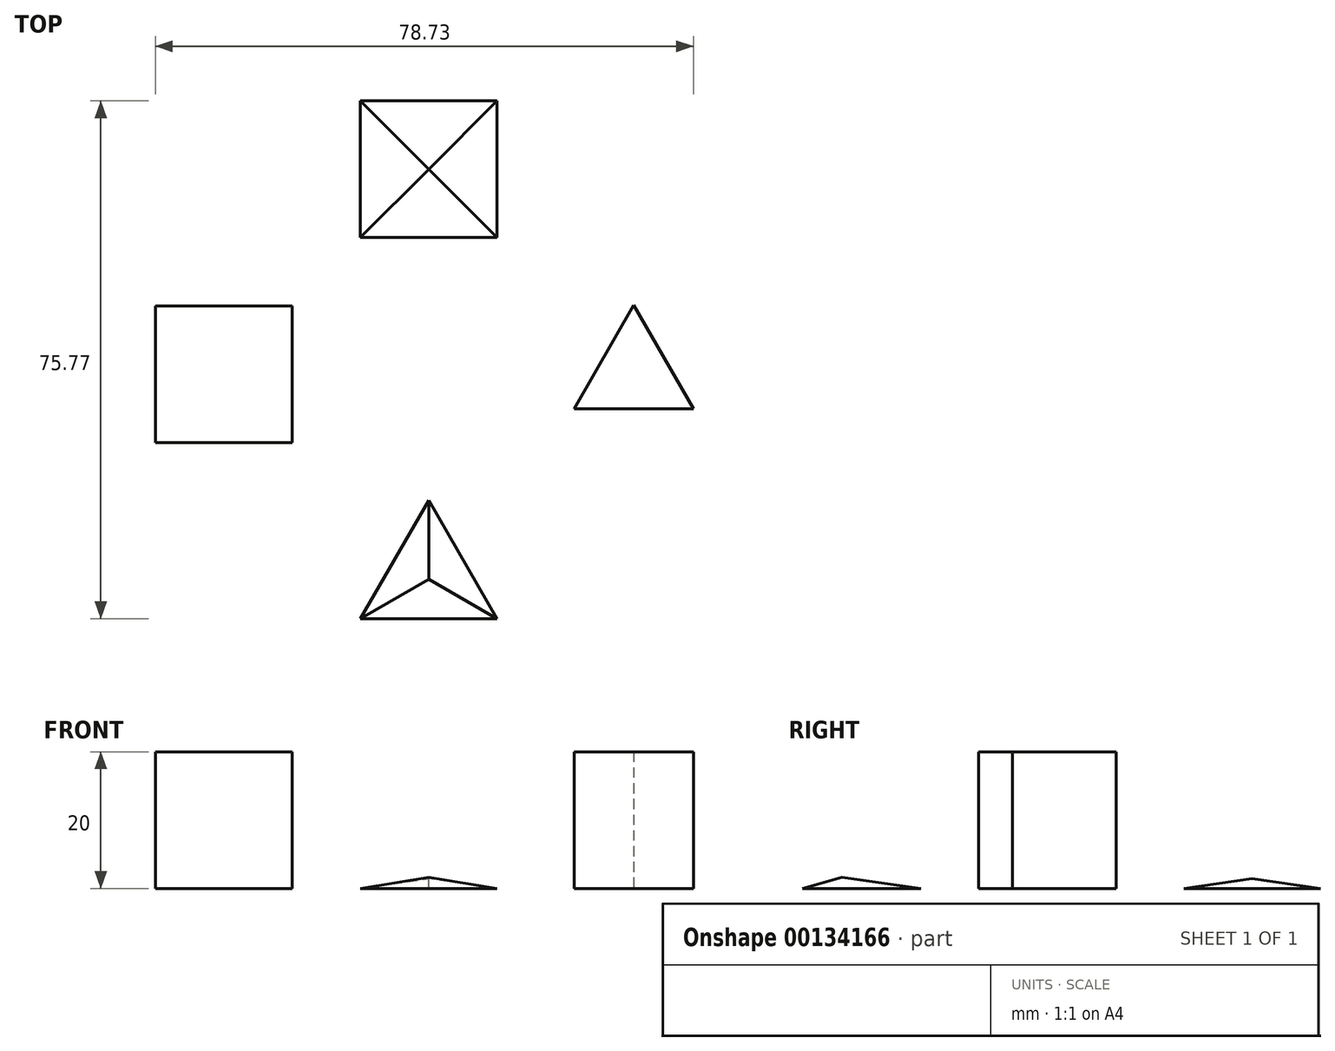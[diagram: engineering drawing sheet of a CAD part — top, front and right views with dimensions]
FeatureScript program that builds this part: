
annotation { "Feature Type Name" : "Feature", "Feature Type Description" : "" }
export const myFeature = defineFeature(function(context is Context, id is Id, definition is map)
    precondition{}
    {
        {
            var Q0;
            Q0=qCreatedBy(makeId("Top.planeOp"),FACE);
            var sketch = newSketch(context, id + "F0", { "sketchPlane" : qUnion([Q0])});
            skLineSegment(sketch, "E0.bottom", {"start": v(-20, 10) * mm, "end": v(-40, 10) * mm});
            skLineSegment(sketch, "E0.top", {"start": v(-20, -10) * mm, "end": v(-40, -10) * mm});
            skLineSegment(sketch, "E0.left", {"start": v(-20, 10) * mm, "end": v(-20, -10) * mm});
            skLineSegment(sketch, "E0.right", {"start": v(-40, 10) * mm, "end": v(-40, -10) * mm});
            skPoint(sketch, "E0.middle", {"position": v(-30, 0) * mm});
            skSolve(sketch);
        }
        {
            var Q0;
            Q0=makeQuery(id+"F0.imprint","IMPRINT",FACE,{"disambiguationData":[TD([[makeQuery(id+"F0.imprint","IMPRINT",EDGE,{"derivedFrom":sQuery(id+"F0.wireOp",EDGE,"E0.bottom")}),1.0]])]});
            extrude(context, id + "F1", {"entities" : qUnion([Q0]), "depth" : 20 * mm});
        }
        {
            var Q0;
            Q0=qCreatedBy(makeId("Top.planeOp"),FACE);
            var sketch = newSketch(context, id + "F2", { "sketchPlane" : qUnion([Q0])});
            skLineSegment(sketch, "E1", {"start": v(-10, -35.77) * mm, "end": v(10, -35.77) * mm});
            skLineSegment(sketch, "E2", {"start": v(10, -35.77) * mm, "end": v(0, -18.45) * mm});
            skLineSegment(sketch, "E3", {"start": v(0, -18.45) * mm, "end": v(-10, -35.77) * mm});
            skCircle(sketch, "E4", {"center": v(0, -30) * mm, "radius": 5.77 * mm});
            skSolve(sketch);
        }
        {
            var Q0;
            Q0=qCreatedBy(makeId("Top.planeOp"),FACE);
            var sketch = newSketch(context, id + "F3", { "sketchPlane" : qUnion([Q0])});
            skLineSegment(sketch, "E5.bottom", {"start": v(10, 40) * mm, "end": v(-10, 40) * mm});
            skLineSegment(sketch, "E5.top", {"start": v(10, 20) * mm, "end": v(-10, 20) * mm});
            skLineSegment(sketch, "E5.left", {"start": v(10, 40) * mm, "end": v(10, 20) * mm});
            skLineSegment(sketch, "E5.right", {"start": v(-10, 40) * mm, "end": v(-10, 20) * mm});
            skPoint(sketch, "E5.middle", {"position": v(0, 30) * mm});
            skSolve(sketch);
        }
        {
            var Q0;
            Q0=qCreatedBy(makeId("Top.planeOp"),FACE);
            var sketch = newSketch(context, id + "F4", { "sketchPlane" : qUnion([Q0])});
            skLineSegment(sketch, "E6", {"start": v(21.27, -5.04) * mm, "end": v(30, 10.08) * mm});
            skLineSegment(sketch, "E7", {"start": v(30, 10.08) * mm, "end": v(38.73, -5.04) * mm});
            skLineSegment(sketch, "E8", {"start": v(38.73, -5.04) * mm, "end": v(21.27, -5.04) * mm});
            skCircle(sketch, "E9", {"center": v(30, 0) * mm, "radius": 5.04 * mm});
            skSolve(sketch);
        }
        {
            var Q0;
            Q0=qCreatedBy(makeId("Top.planeOp"),FACE);
            cPlane(context, id + "F5", {"entities" : qUnion([Q0]), "cplaneType" : CPlaneType.OFFSET, "offset" : (2 / 3 * sqrt(6)) * mm, "width" : 150 * mm, "height" : 150 * mm});
        }
        {
            var Q0;
            Q0=qCreatedBy(makeId("Top.planeOp"),FACE);
            cPlane(context, id + "F6", {"entities" : qUnion([Q0]), "cplaneType" : CPlaneType.OFFSET, "offset" : (sqrt(2)) * mm, "width" : 150 * mm, "height" : 150 * mm});
        }
        {
            var Q0;
            Q0=qCreatedBy(id+"F5.planeOp",FACE);
            var sketch = newSketch(context, id + "F7", { "sketchPlane" : qUnion([Q0])});
            skPoint(sketch, "E10", {"position": v(0, -30) * mm});
            skSolve(sketch);
        }
        {
            var Q0;
            Q0=qCreatedBy(id+"F6.planeOp",FACE);
            var sketch = newSketch(context, id + "F8", { "sketchPlane" : qUnion([Q0])});
            skPoint(sketch, "E11", {"position": v(0, 30) * mm});
            skSolve(sketch);
        }
        {
            var Q0;
            Q0 = qSketchRegion(id + "F4", true);
            extrude(context, id + "F9", {"entities" : qUnion([Q0]), "depth" : 20 * mm});
        }
        {
            var Q0;
            Q0=makeQuery(id+"F3.imprint","IMPRINT",FACE,{"disambiguationData":[TD([[makeQuery(id+"F3.imprint","IMPRINT",EDGE,{"derivedFrom":sQuery(id+"F3.wireOp",EDGE,"E5.bottom")}),1.0]])]});
            var Q1;
            Q1=sQuery(id+"F8.wireOp",VERTEX,"E11");
            loft(context, id + "F10", {"sheetProfilesArray" : [{ "sheetProfileEntities" : qUnion([Q0]) }, { "sheetProfileEntities" : qUnion([Q1]) }]});
        }
        {
            var Q0;
            Q0 = qSketchRegion(id + "F2", true);
            var Q1;
            Q1=sQuery(id+"F7.wireOp",VERTEX,"E10");
            loft(context, id + "F11", {"sheetProfilesArray" : [{ "sheetProfileEntities" : qUnion([Q0]) }, { "sheetProfileEntities" : qUnion([Q1]) }]});
        }
    });
